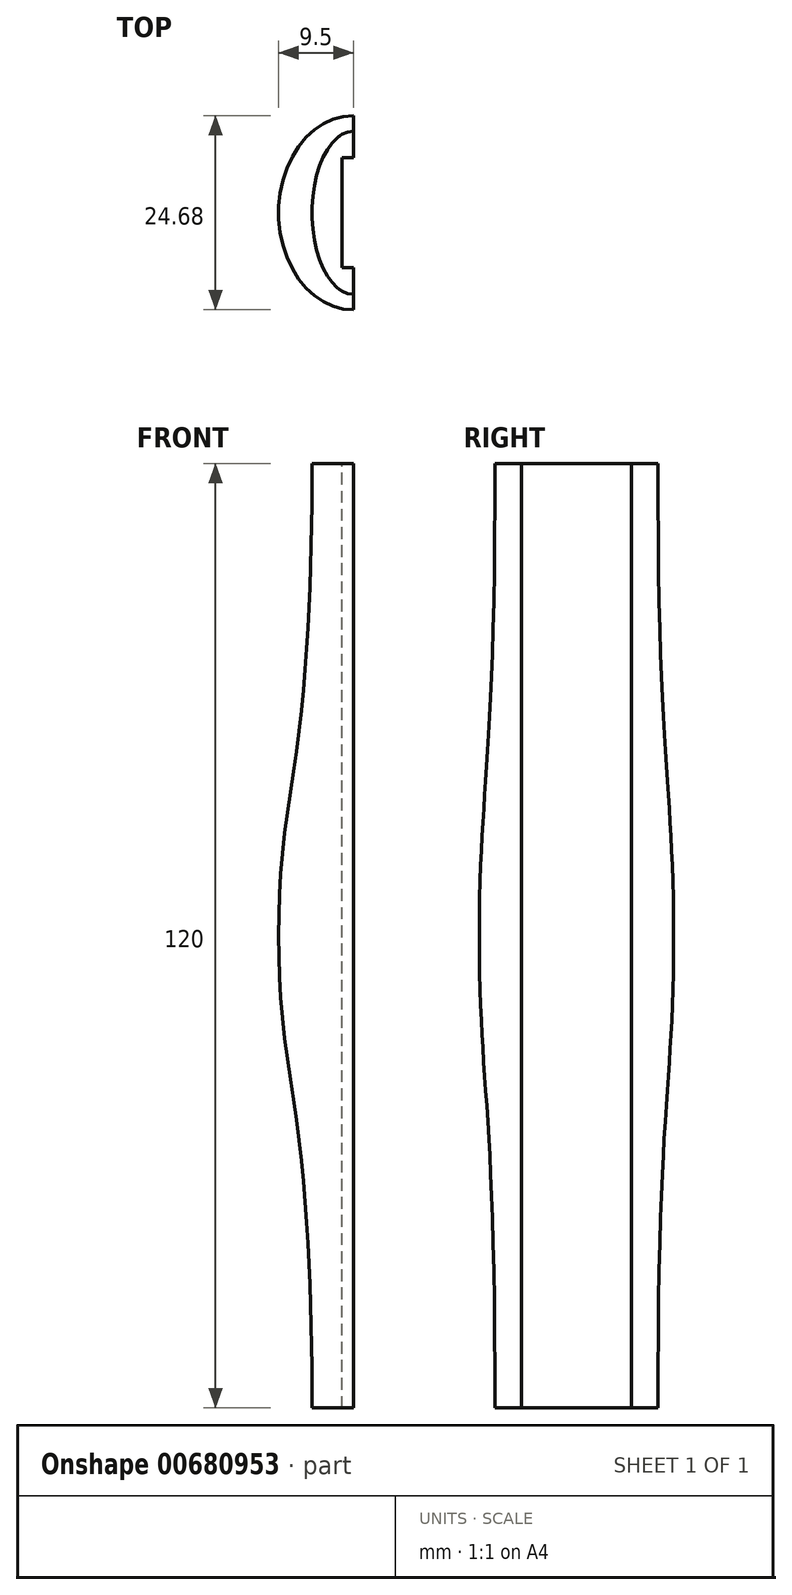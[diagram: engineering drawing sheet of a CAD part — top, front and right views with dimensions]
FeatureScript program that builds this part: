
annotation { "Feature Type Name" : "Feature", "Feature Type Description" : "" }
export const myFeature = defineFeature(function(context is Context, id is Id, definition is map)
    precondition{}
    {
        {
            var Q0;
            Q0=qCreatedBy(makeId("Top.planeOp"),FACE);
            var sketch = newSketch(context, id + "F0", { "sketchPlane" : qUnion([Q0])});
            skEllipticalArc(sketch, "E0", {});
            skLineSegment(sketch, "E1", {"start": v(0, -12.34) * mm, "end": v(0, 12.34) * mm});
            const initialGuessF0  = {"E0": [0, 0, 0, -1, 0.012335, 0.0095, 3.141592653589793, 0]};
            skSetInitialGuess(sketch, initialGuessF0);
            skSolve(sketch);
        }
        {
            var Q0;
            Q0=qCreatedBy(makeId("Top.planeOp"),FACE);
            cPlane(context, id + "F1", {"entities" : qUnion([Q0]), "cplaneType" : CPlaneType.OFFSET, "offset" : 60 * mm, "width" : 150 * mm, "height" : 150 * mm});
        }
        {
            var Q0;
            Q0=qCreatedBy(id+"F1.planeOp",FACE);
            var sketch = newSketch(context, id + "F2", { "sketchPlane" : qUnion([Q0])});
            skEllipticalArc(sketch, "E2", {});
            skLineSegment(sketch, "E3", {"start": v(0, 10.35) * mm, "end": v(0, -10.35) * mm});
            const initialGuessF2  = {"E2": [0, 0, 0, -1, 0.01035, 0.00525, 3.141592653589793, 0]};
            skSetInitialGuess(sketch, initialGuessF2);
            skSolve(sketch);
        }
        {
            var Q0;
            Q0=makeQuery(id+"F0.imprint","IMPRINT",FACE,{"disambiguationData":[TD([[makeQuery(id+"F0.imprint","IMPRINT",EDGE,{"derivedFrom":sQuery(id+"F0.wireOp",EDGE,"E0")}),1.0]])]});
            var Q1;
            Q1=makeQuery(id+"F2.imprint","IMPRINT",FACE,{"disambiguationData":[TD([[makeQuery(id+"F2.imprint","IMPRINT",EDGE,{"derivedFrom":sQuery(id+"F2.wireOp",EDGE,"E2")}),1.0]])]});
            loft(context, id + "F3", {"startCondition" : LoftEndDerivativeType.NORMAL_TO_PROFILE, "startMagnitude" : 1, "endCondition" : LoftEndDerivativeType.NORMAL_TO_PROFILE, "endMagnitude" : 2, "sheetProfilesArray" : [{ "sheetProfileEntities" : qUnion([Q0]) }, { "sheetProfileEntities" : qUnion([Q1]) }]});
        }
        {
            var Q0;
            Q0=makeQuery(id+"F3.opLoft","SWEPT_BODY",BODY,{"disambiguationData":[OSD([makeQuery(id+"F0.imprint","IMPRINT",FACE,{"disambiguationData":[TD([[makeQuery(id+"F0.imprint","IMPRINT",EDGE,{"derivedFrom":sQuery(id+"F0.wireOp",EDGE,"E0")}),1.0]])]}),makeQuery(id+"F2.imprint","IMPRINT",FACE,{"disambiguationData":[TD([[makeQuery(id+"F2.imprint","IMPRINT",EDGE,{"derivedFrom":sQuery(id+"F2.wireOp",EDGE,"E2")}),1.0]])]})])]});
            var Q1;
            Q1=qCreatedBy(makeId("Top.planeOp"),FACE);
            mirror(context, id + "F4", {"operationType" : NewBodyOperationType.ADD, "entities" : qUnion([Q0]), "mirrorPlane" : qUnion([Q1])});
        }
        {
            var Q0;
            Q0=makeQuery(id+"F3.opLoft","CAP_FACE",FACE,{"disambiguationData":[OSD([makeQuery(id+"F2.imprint","IMPRINT",FACE,{"disambiguationData":[TD([[makeQuery(id+"F2.imprint","IMPRINT",EDGE,{"derivedFrom":sQuery(id+"F2.wireOp",EDGE,"E2")}),1.0]])]})])],"isStart":true});
            var sketch = newSketch(context, id + "F5", { "sketchPlane" : qUnion([Q0])});
            skLineSegment(sketch, "E4.bottom", {"start": v(-1.43, 7) * mm, "end": v(1.44, 7) * mm});
            skLineSegment(sketch, "E4.top", {"start": v(-1.44, -7) * mm, "end": v(1.43, -7) * mm});
            skLineSegment(sketch, "E4.left", {"start": v(-1.43, 7) * mm, "end": v(-1.44, -7) * mm});
            skLineSegment(sketch, "E4.right", {"start": v(1.44, 7) * mm, "end": v(1.43, -7) * mm});
            skPoint(sketch, "E4.middle", {"position": v(0, 0) * mm});
            skSolve(sketch);
        }
        {
            var Q0;
            Q0=qSketchRegion(id+"F5",true);
            extrude(context, id + "F6", {"entities" : qUnion([Q0]), "operationType" : NewBodyOperationType.REMOVE, "oppositeDirection" : true, "depth" : 120 * mm, "offsetDistance" : 25 * mm});
        }
    });
